# Revit family: BDG_BossDesign_Stng_ATOM_IndividualUnit
name_source: partatom
category: Furniture
revit_build: Autodesk Revit 2015 (Build: 20140903_1530(x64)
units: mm (PartAtom-declared; Revit-internal decimal feet)

## types (10) — shared parameters
Assembly Code = E2020200
AssetType = Movable
BIMObjectName = BDG_BossDesign_Seating_ATOM_IndividualUnit
BaseMaterial = BDG_Generic_Metal_Steel_RAL7043TrafficGrey
Category = Pr_40_50_12 : Chairs, seats and benches
DurationUnit = year
ExpectedLife = 5
Finish = Fabric
IfcExportAs = IfcFurnishingElementType
IfcExportType = SOFA
Keynote = Pr_40_50_12
ManufacturerName = Boss Design
ManufacturerURL = www.bossdesign.com
Material = Upholstered
NBSDescription = Seating
NBSReference = 45-35-72/352
Name = Seating_ATOM_IndividualUnit_BossDesign
URL = www.bossdesign.com
Uniclass2015Code = Pr_40_50_12
Uniclass2015Title = Chairs, seats and benches
Uniclass2015Version = Products v1.9
Version = 1
WarrantyDescription = Structural Warranty Excludes Foams and Fabrics
WarrantyDurationLabor = 5
WarrantyDurationParts = 5
WarrantyDurationUnit = year

## per-type parameters (varying)
| type | Description | IsATO00 | IsATO00H | IsATO00L | IsATO15IS | IsATO15ISH | IsATO15ISL | IsATO30IS | IsATO30ISH | IsATO30ISL | IsATO45ES | IsATO45ESH | IsATO45ESL | IsATO45IS | IsATO45ISH | IsATO45ISL | IsHighBack | IsLowBack | ModelReference | NominalHeight | NominalLength | NominalWidth | Shape | Size |
| ATO/45/ES/H | ATOM High Back 45° Curved Seating Unit | No | No | No | No | No | No | No | No | No | Yes | Yes | No | No | No | No | Yes | No | ATOM High Back 45° Curved Seating Unit | 1390 mm | 1080 mm | 870 mm | Curved | 1080 x 870 x 1390mm |
| ATO/45/ES/L | ATOM Low Back 45° Curved Seating Unit | No | No | No | No | No | No | No | No | No | Yes | No | Yes | No | No | No | No | Yes | ATOM Low Back 45° Curved Seating Unit | 1010 mm | 1080 mm | 810 mm | Curved | 1080 x 810 x 1010mm |
| ATO/00/H | ATOM High Back Seating Unit | Yes | Yes | No | No | No | No | No | No | No | No | No | No | No | No | No | Yes | No | ATOM High Back Seating Unit | 1390 mm | 1100 mm | 780 mm | Rectangular | 1100 x 780 x 1390mm |
| ATO/00/L | ATOM Low Back Seating Unit | Yes | No | Yes | No | No | No | No | No | No | No | No | No | No | No | No | No | Yes | ATOM Low Back Seating Unit | 1010 mm | 1100 mm | 730 mm | Rectangular | 1100 x 730 x 1010mm |
| ATO/15/IS/H | ATOM High Back 15° Curved Seating Unit | No | No | No | Yes | Yes | No | No | No | No | No | No | No | No | No | No | Yes | No | ATOM High Back 15° Curved Seating Unit | 1390 mm | 1110 mm | 805 mm | Curved | 1110 x 805 x1390mm |
| ATO/15/IS/L | ATOM Low Back 15° Curved Seating Unit | No | No | No | Yes | No | Yes | No | No | No | No | No | No | No | No | No | No | Yes | ATOM Low Back 15° Curved Seating Unit | 1010 mm | 1095 mm | 750 mm | Curved | 1095 x 750 x1010mm |
| ATO/30/IS/H | ATOM High Back 30° Curved Seating Unit | No | No | No | No | No | No | Yes | Yes | No | No | No | No | No | No | No | Yes | No | ATOM High Back 30° Curved Seating Unit | 1390 mm | 1125 mm | 820 mm | Curved | 1125 x 820 x 1390mm |
| ATO/30/IS/L | ATOM Low Back 30° Curved Seating Unit | No | No | No | No | No | No | Yes | No | Yes | No | No | No | No | No | No | No | Yes | ATOM Low Back 30° Curved Seating Unit | 1010 mm | 1095 mm | 765 mm | Curved | 1095 x 765 x 1010mm |
| ATO/45/IS/H | ATOM High Back 45° Curved Seating Unit | No | No | No | No | No | No | No | No | No | No | No | No | Yes | Yes | No | Yes | No | ATOM High Back 45° Curved Seating Unit | 1390 mm | 1135 mm | 835 mm | Curved | 1135 x 835 x 1390mm |
| ATO/45/IS/L | ATOM Low Back 45° Curved Seating Unit | No | No | No | No | No | No | No | No | No | No | No | No | Yes | No | Yes | No | Yes | ATOM Low Back 45° Curved Seating Unit | 1010 mm | 1090 mm | 795 mm | Curved | 1090 x 795 x 1010mm |

note: column(s) folded — value = type name in every type: Model, ModelNumber

## geometry (parser evidence)
native form markers: Sweep x3
no freeform markers — native parametric forms only
